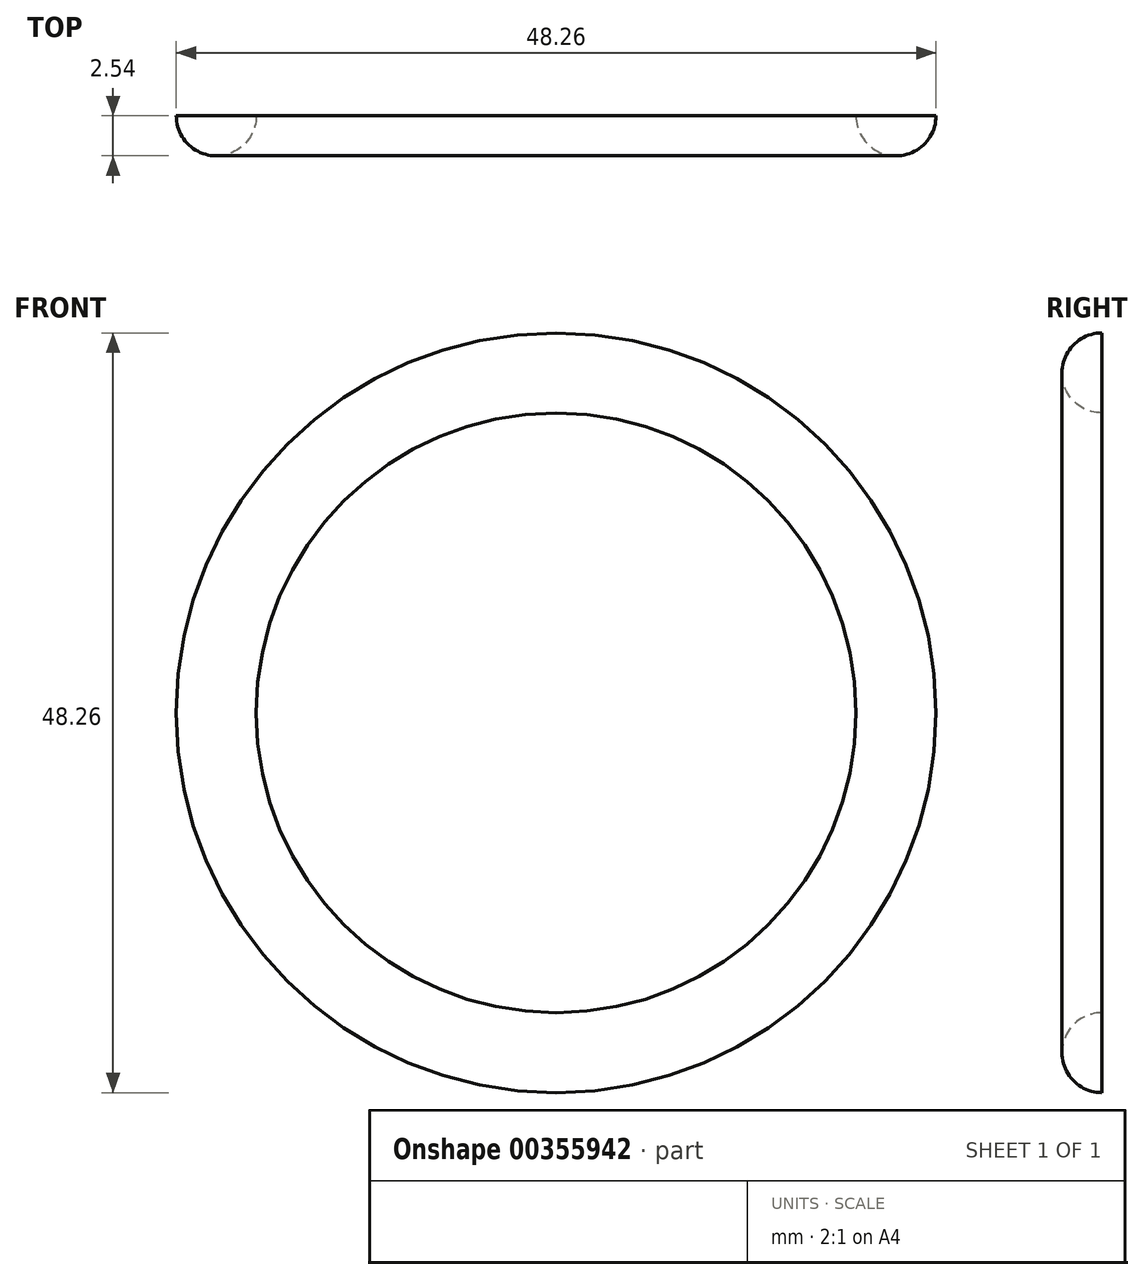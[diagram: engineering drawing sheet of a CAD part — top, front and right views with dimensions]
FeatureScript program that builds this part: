
annotation { "Feature Type Name" : "Feature", "Feature Type Description" : "" }
export const myFeature = defineFeature(function(context is Context, id is Id, definition is map)
    precondition{}
    {
        {
            var Q0;
            Q0=qCreatedBy(makeId("Front.planeOp"),FACE);
            var sketch = newSketch(context, id + "F0", { "sketchPlane" : qUnion([Q0])});
            skCircle(sketch, "E0", {"center": v(0, 0) * mm, "radius": 19.05 * mm});
            skSolve(sketch);
        }
        {
            var Q0;
            Q0=qCreatedBy(makeId("Right.planeOp"),FACE);
            var sketch = newSketch(context, id + "F1", { "sketchPlane" : qUnion([Q0])});
            skArc(sketch, "E1", {"start": v(0, 24.13) * mm, "mid": v(-2.54, 21.59) * mm, "end": v(0, 19.05) * mm});
            skLineSegment(sketch, "E2", {"start": v(0, 24.13) * mm, "end": v(0, 19.05) * mm});
            skSolve(sketch);
        }
        {
            var Q0;
            Q0=qSketchRegion(id+"F1",true);
            var Q1;
            Q1=sQuery(id+"F0.wireOp",EDGE,"E0");
            revolve(context, id + "F2", {"entities" : qUnion([Q0]), "axis" : qUnion([Q1]), "revolveType" : RevolveType.FULL});
        }
    });
